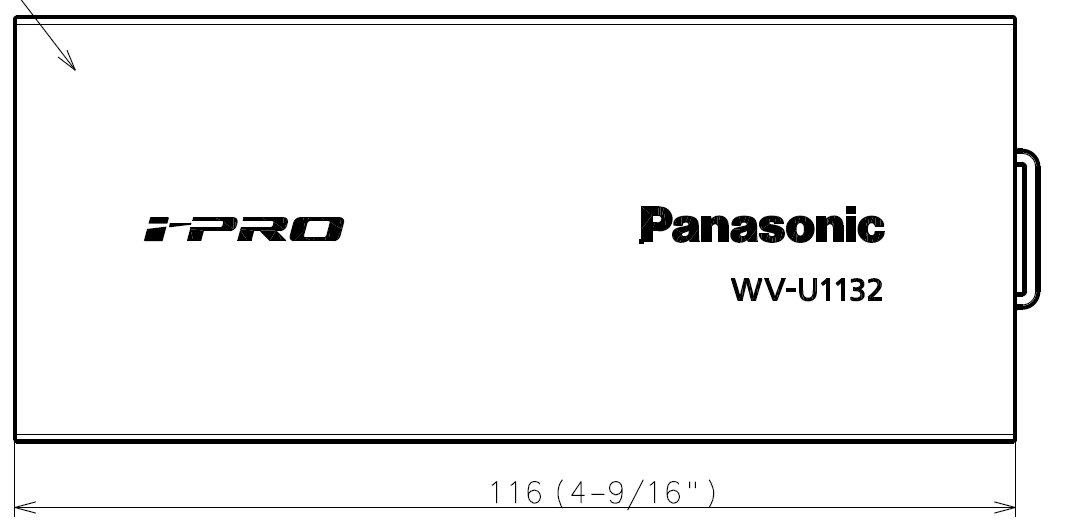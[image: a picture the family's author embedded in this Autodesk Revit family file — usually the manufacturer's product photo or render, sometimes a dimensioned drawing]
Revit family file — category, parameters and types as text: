
# Revit family: Camera-Security-Panasonic-Super_Dynamic-H265_Varifocal-Network-Fixed_Box-WV-U1132SeriesX
name_source: partatom
category: Security Devices
units: mm (PartAtom-declared; Revit-internal decimal feet)

## family parameters
Always vertical = No
Cut with Voids When Loaded = No
Maintain Annotation Orientation = No
OmniClass Number = 23.85.10.14.11
OmniClass Title = Cameras
Part Type = Normal
Room Calculation Point = No
Round Connector Dimension = Use Diameter
Shared = No
Work Plane-Based = Yes

## types (3) — shared parameters
Auto Back Focus = No
Body Radius = 1.161 "
Communication Ports = 10Base-T / 100Base-TX, RJ45 connector
Day Or Night = Yes
Default Elevation = 48 "
Depth = 4.567 "
Equipment Abbreviation = SC
Family Version = 1.0.0
Has POE = Yes
Height = 1.929 "
IP Or Analog = IP
Indoor Or Outdoor = Indoor
Manufacturer = Panasonic
Model Disclaimer = Contact Panasonic for more information
Mounting Positions = Mount Dependent
On Wall = Yes
Operational Humidity = 10 to 90 % (no condensation)
Operational Temperature = -10 °C to +50 °C (+14 °F to +122 °F)
Pan Angle Fixed = 0.00°
Product Documentation Link = https://bizpartner.panasonic.net
Product Material = Paint - Panasonic - i-PRO White
Product Page URL = https://security.panasonic.com
Provide Feedback = https://www.surveymonkey.com
Regulatory Compliance = UL (UL60950-1), c-UL (CSA C22.2 No.60950-1), CE, IEC60950-1, FCC (Part15 ClassA), ICES003 ClassA, EN55032 ClassB, EN55024
Storage Temperature = -10 °C to +50 °C (+14 °F to +122 °F)
Til Angle Fixed = 0.00°
URL = http://security.panasonic.com
VV Origin Height = 4.244 "
Vandal Resistant = No
Voltage DC = 48 V
Wide Dynamic Range = Yes
Width = 2.323 "
Yaw Angle Fixed = 0.00°
zero-valued in all types: VV Viewpoint Depth Max, VV Viewpoint Depth Min

## per-type parameters (varying)
| type | Angle Of View | Camera Type | Date Last Modified | Description | HFOV Max 169 | HFOV Max 43 | HFOV Min 169 | HFOV Min 43 | Minimum Illumination | Model | Part Description | Part Number | VFOV Max 169 | VFOV Max 43 | VFOV Min 169 | VFOV Min 43 | Weight |
| Full HD, WV-U1132 | 102 | 1 | 2020/01/06 | Security Camera, Network, Super Dynamic, Full HD, iA, Full HD, H.265 Varifocal Camera, WV-U1132 | 102.00° | 84.00° | 44.00° | 36.00° | 0.100 lx | WV-U1132 | Security Camera, Network, Super Dynamic, Full HD, iA, Full HD, H.265 Varifocal Camera, WV-U1132 | WV-U1132 | 56.00° | 63.00° | 24.00° | 27.00° | 0.34 lb |
| 4M Pixel, WV-U1142 | 103 | 2 | 2020/01/06 | Security Camera, Network, Super Dynamic, 4M Pixel, iA, H.265 Varifocal Camera, WV-U1142 | 103.00° | 103.00° | 44.00° | 44.00° | 0.300 lx | WV-U1142 | Security Camera, Network, Super Dynamic, 4M Pixel, iA, H.265 Varifocal Camera, WV-U1142 | WV-U1142 | 57.00° | 57.00° | 25.00° | 25.00° | 0.44 lb |
| Full HD, WV-U1130 | 102 | 3 | 2020/04/06 | Security Camera, Super Dynamic, Full HD, iA, Full HD, H.265 Network Camera, WV-U1130 | 102.00° | 83.00° | 102.00° | 83.00° | 0.100 lx | WV-U1130 | Security Camera, Super Dynamic, Full HD, iA, Full HD, H.265 Network Camera, WV-U1130 | WV-U1130 | 55.00° | 61.00° | 55.00° | 61.00° | 0.33 lb |

## geometry (parser evidence)
native form markers: Blend x2, Sweep x2
no freeform markers — native parametric forms only
